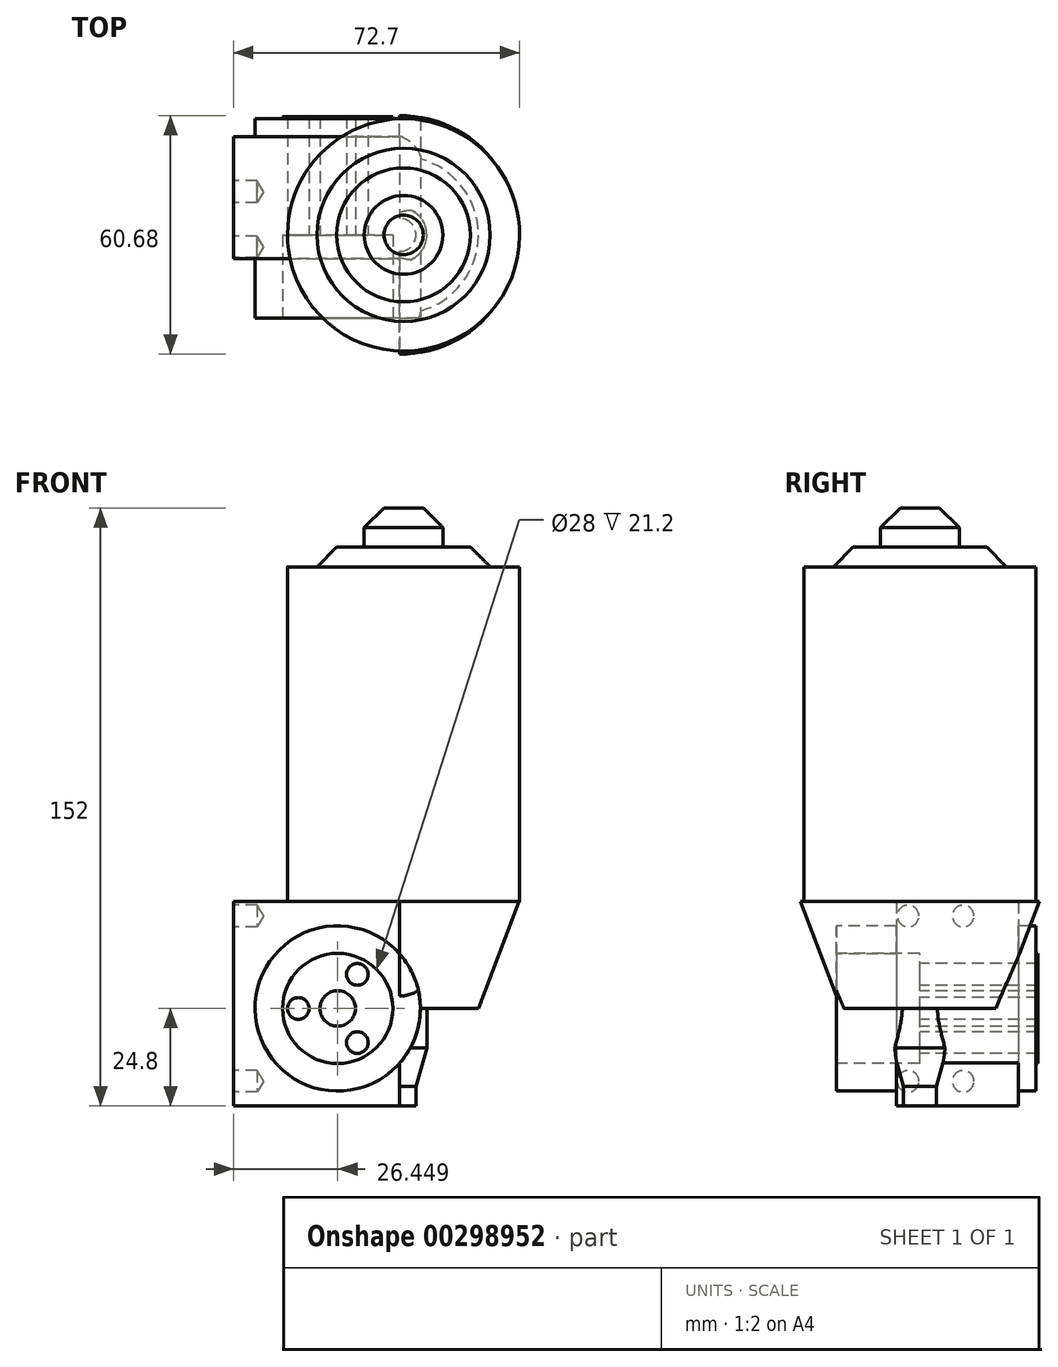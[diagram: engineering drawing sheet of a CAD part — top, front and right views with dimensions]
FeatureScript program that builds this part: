
annotation { "Feature Type Name" : "Feature", "Feature Type Description" : "" }
export const myFeature = defineFeature(function(context is Context, id is Id, definition is map)
    precondition{}
    {
        {
            var Q0;
            Q0=qCreatedBy(makeId("Top.planeOp"),FACE);
            var sketch = newSketch(context, id + "F0", { "sketchPlane" : qUnion([Q0])});
            skCircle(sketch, "E0", {"center": v(0, 0) * mm, "radius": 29.5 * mm});
            skCircle(sketch, "E1", {"center": v(0, 0) * mm, "radius": 22 * mm});
            skCircle(sketch, "E2", {"center": v(0, 0) * mm, "radius": 10 * mm});
            skSolve(sketch);
        }
        {
            var Q0;
            Q0=makeQuery(id+"F0.imprint","IMPRINT",FACE,{"disambiguationData":[TD([[makeQuery(id+"F0.imprint","IMPRINT",EDGE,{"derivedFrom":sQuery(id+"F0.wireOp",EDGE,"E2")}),1.0]])]});
            extrude(context, id + "F1", {"entities" : qUnion([Q0]), "depth" : 100 * mm});
        }
        {
            var Q0;
            Q0=makeQuery(id+"F0.imprint","IMPRINT",FACE,{"disambiguationData":[TD([[makeQuery(id+"F0.imprint","IMPRINT",EDGE,{"derivedFrom":sQuery(id+"F0.wireOp",EDGE,"E1")}),1.0]])]});
            extrude(context, id + "F2", {"entities" : qUnion([Q0]), "operationType" : NewBodyOperationType.ADD, "depth" : 90 * mm});
        }
        {
            var Q0;
            Q0=makeQuery(id+"F0.imprint","IMPRINT",FACE,{"disambiguationData":[TD([[makeQuery(id+"F0.imprint","IMPRINT",EDGE,{"derivedFrom":sQuery(id+"F0.wireOp",EDGE,"E0")}),1.0]])]});
            extrude(context, id + "F3", {"entities" : qUnion([Q0]), "operationType" : NewBodyOperationType.ADD, "depth" : 85 * mm});
        }
        {
            var Q0;
            Q0=makeQuery(id+"F2.opExtrude","CAP_EDGE",EDGE,{"disambiguationData":[OSD([sQuery(id+"F0.wireOp",EDGE,"E1")])],"isStart":false});
            chamfer(context, id + "F4", {"entities" : qUnion([Q0]), "width" : 5 * mm, "tangentPropagation" : true});
        }
        {
            var Q0;
            Q0=makeQuery(id+"F1.opExtrude","CAP_EDGE",EDGE,{"disambiguationData":[OSD([sQuery(id+"F0.wireOp",EDGE,"E2")])],"isStart":false});
            chamfer(context, id + "F5", {"entities" : qUnion([Q0]), "width" : 5 * mm, "tangentPropagation" : true});
        }
        {
            var Q0;
            Q0=qCreatedBy(makeId("Front.planeOp"),FACE);
            var sketch = newSketch(context, id + "F6", { "sketchPlane" : qUnion([Q0])});
            skCircle(sketch, "E3", {"center": v(-16.75, -27.2) * mm, "radius": 4.5 * mm});
            skCircle(sketch, "E4", {"center": v(-16.75, -27.2) * mm, "radius": 14 * mm});
            skPoint(sketch, "E5", {"position": v(-26.75, -27.2) * mm});
            skPoint(sketch, "E6", {"position": v(-11.75, -35.86) * mm});
            skPoint(sketch, "E7", {"position": v(-11.75, -18.54) * mm});
            skLineSegment(sketch, "E8", {"start": v(-16.75, -27.2) * mm, "end": v(-0.15, -55.96) * mm, "construction": true});
            skLineSegment(sketch, "E9", {"start": v(-16.75, -27.2) * mm, "end": v(-44.95, -27.2) * mm, "construction": true});
            skLineSegment(sketch, "E10", {"start": v(-16.75, -27.2) * mm, "end": v(-4.8, -6.5) * mm, "construction": true});
            skLineSegment(sketch, "E11.bottom", {"start": v(-43.2, 0) * mm, "end": v(-1, 0) * mm});
            skLineSegment(sketch, "E11.top", {"start": v(-43.2, -52) * mm, "end": v(-1, -52) * mm});
            skLineSegment(sketch, "E11.left", {"start": v(-43.2, 0) * mm, "end": v(-43.2, -52) * mm});
            skLineSegment(sketch, "E11.right", {"start": v(-1, 0) * mm, "end": v(-1, -52) * mm});
            skLineSegment(sketch, "E12", {"start": v(-1, -27.2) * mm, "end": v(19, -27.2) * mm});
            skLineSegment(sketch, "E13", {"start": v(19, -27.2) * mm, "end": v(29.34, 0) * mm});
            skLineSegment(sketch, "E14", {"start": v(29.34, 0) * mm, "end": v(-1, 0) * mm});
            skLineSegment(sketch, "E15", {"start": v(5.9, -27.2) * mm, "end": v(5.9, -37.2) * mm});
            skLineSegment(sketch, "E16", {"start": v(5.9, -37.2) * mm, "end": v(3.16, -47) * mm});
            skLineSegment(sketch, "E17", {"start": v(3.16, -47) * mm, "end": v(3.16, -52) * mm});
            skLineSegment(sketch, "E18", {"start": v(3.16, -52) * mm, "end": v(-1, -52) * mm});
            skCircle(sketch, "E19", {"center": v(-16.75, -27.2) * mm, "radius": 21 * mm});
            skSolve(sketch);
        }
        {
            var Q0;
            {var subQ1=sQuery(id+"F6.wireOp",EDGE,"E11.bottom");Q0=makeQuery(id+"F6.imprint","IMPRINT",FACE,{"disambiguationData":[TD([[makeQuery(id+"F6.imprint","IMPRINT",EDGE,{"derivedFrom":subQ1}),-1.0]])]});}
            extrude(context, id + "F7", {"entities" : qUnion([Q0]), "operationType" : NewBodyOperationType.ADD, "oppositeDirection" : true, "depth" : 25 * mm, "hasSecondDirection" : true, "secondDirectionOppositeDirection" : false, "secondDirectionDepth" : 6 * mm});
        }
        {
            var Q0;
            Q0=makeQuery(id+"F6.imprint","IMPRINT",FACE,{"disambiguationData":[TD([[makeQuery(id+"F6.imprint","IMPRINT",EDGE,{"derivedFrom":sQuery(id+"F6.wireOp",EDGE,"E4")}),-1.0]])]});
            var Q1;
            {var subQ0=sQuery(id+"F6.wireOp",EDGE,"E12");var subQ1=sQuery(id+"F6.wireOp",EDGE,"E11.right");var subQ2=makeQuery(id+"F6.imprint","INTERSECT",VERTEX,{"derivedFrom":[subQ1,subQ0]});Q1=makeQuery(id+"F6.imprint","IMPRINT",FACE,{"disambiguationData":[TD([[makeQuery(id+"F6.imprint","IMPRINT",EDGE,{"disambiguationData":[TD([[subQ2,1.0]])],"derivedFrom":subQ1}),1.0]])]});}
            var Q2;
            {var subQ0=sQuery(id+"F6.wireOp",EDGE,"E12");var subQ1=sQuery(id+"F6.wireOp",EDGE,"E11.right");var subQ2=makeQuery(id+"F6.imprint","INTERSECT",VERTEX,{"derivedFrom":[subQ1,subQ0]});Q2=makeQuery(id+"F6.imprint","IMPRINT",FACE,{"disambiguationData":[TD([[makeQuery(id+"F6.imprint","IMPRINT",EDGE,{"disambiguationData":[TD([[subQ2,-1.0]])],"derivedFrom":subQ1}),1.0]])]});}
            extrude(context, id + "F8", {"entities" : qUnion([Q0, Q1, Q2]), "operationType" : NewBodyOperationType.ADD, "oppositeDirection" : true, "depth" : 29.5 * mm, "hasSecondDirection" : true, "secondDirectionOppositeDirection" : false, "secondDirectionDepth" : 21.2 * mm});
        }
        {
            var Q0;
            Q0=makeQuery(id+"F6.imprint","IMPRINT",FACE,{"disambiguationData":[TD([[makeQuery(id+"F6.imprint","IMPRINT",EDGE,{"derivedFrom":sQuery(id+"F6.wireOp",EDGE,"E3")}),-1.0]])]});
            extrude(context, id + "F9", {"entities" : qUnion([Q0]), "operationType" : NewBodyOperationType.ADD, "oppositeDirection" : true, "depth" : 30 * mm});
        }
        {
            var Q0;
            {var subQ0=sQuery(id+"F6.wireOp",EDGE,"E13");Q0=makeQuery(id+"F6.imprint","IMPRINT",FACE,{"disambiguationData":[TD([[makeQuery(id+"F6.imprint","IMPRINT",EDGE,{"derivedFrom":subQ0}),1.0]])]});}
            var Q1;
            {var subQ0=sQuery(id+"F6.wireOp",EDGE,"E15");Q1=makeQuery(id+"F6.imprint","IMPRINT",FACE,{"disambiguationData":[TD([[makeQuery(id+"F6.imprint","IMPRINT",EDGE,{"derivedFrom":subQ0}),-1.0]])]});}
            var Q2;
            Q2=sQuery(id+"F6.wireOp",EDGE,"E11.right");
            revolve(context, id + "F10", {"operationType" : NewBodyOperationType.ADD, "entities" : qUnion([Q0, Q1]), "axis" : qUnion([Q2]), "revolveType" : RevolveType.SYMMETRIC, "angle" : 180 * degree});
        }
        {
            var Q0;
            Q0=sQuery(id+"F6.wireOp",VERTEX,"E5");
            var Q1;
            Q1=sQuery(id+"F6.wireOp",VERTEX,"E6");
            var Q2;
            Q2=sQuery(id+"F6.wireOp",VERTEX,"E7");
            var Q3;
            Q3=makeQuery(id+"F1.opExtrude","SWEPT_BODY",BODY,{"disambiguationData":[OSD([sQuery(id+"F0.wireOp",EDGE,"E2")])]});
            hole(context, id + "F11", {"style" : HoleStyle.SIMPLE, "endStyle" : HoleEndStyle.THROUGH, "standardTappedOrClearance" : lookupTablePath({ "standard" : "ISO", "fit" : "Normal", "size" : "M5", "type" : "Clearance" }), "standardBlindInLast" : lookupTablePath({ "fit" : "Standard", "standard" : "ISO", "size" : "M5", "type" : "Clearance" }), "holeDiameter" : 5.5 * mm, "isTappedThrough" : true, "tappedDepth" : 12 * mm, "tapClearance" : 3, "locations" : qUnion([Q0, Q1, Q2]), "scope" : qUnion([Q3])});
        }
        {
            var Q0;
            Q0=makeQuery(id+"F7.opExtrude","SWEPT_FACE",FACE,{"disambiguationData":[OSD([sQuery(id+"F6.wireOp",EDGE,"E11.left")])]});
            var sketch = newSketch(context, id + "F12", { "sketchPlane" : qUnion([Q0])});
            skPoint(sketch, "E20", {"position": v(-11, -3.7) * mm});
            skPoint(sketch, "E21", {"position": v(3, -3.7) * mm});
            skPoint(sketch, "E22", {"position": v(3, -45.7) * mm});
            skPoint(sketch, "E23", {"position": v(-11, -45.7) * mm});
            skLineSegment(sketch, "E24", {"start": v(30.35, -27.2) * mm, "end": v(-37.12, -27.2) * mm, "construction": true});
            skSolve(sketch);
        }
        {
            var Q0;
            Q0=sQuery(id+"F12.wireOp",VERTEX,"E20");
            var Q1;
            Q1=sQuery(id+"F12.wireOp",VERTEX,"E21");
            var Q2;
            Q2=sQuery(id+"F12.wireOp",VERTEX,"E22");
            var Q3;
            Q3=sQuery(id+"F12.wireOp",VERTEX,"E23");
            var Q4;
            Q4=makeQuery(id+"F1.opExtrude","SWEPT_BODY",BODY,{"disambiguationData":[OSD([sQuery(id+"F0.wireOp",EDGE,"E2")])]});
            hole(context, id + "F13", {"style" : HoleStyle.SIMPLE, "endStyle" : HoleEndStyle.BLIND, "standardTappedOrClearance" : lookupTablePath({ "standard" : "ISO", "fit" : "Normal", "size" : "M5", "type" : "Clearance" }), "standardBlindInLast" : lookupTablePath({ "fit" : "Standard", "standard" : "ISO", "size" : "M5", "type" : "Clearance" }), "holeDiameter" : 5.5 * mm, "holeDepth" : 6 * mm, "isTappedThrough" : true, "tappedDepth" : 12 * mm, "tapClearance" : 3, "locations" : qUnion([Q0, Q1, Q2, Q3]), "scope" : qUnion([Q4])});
        }
    });
